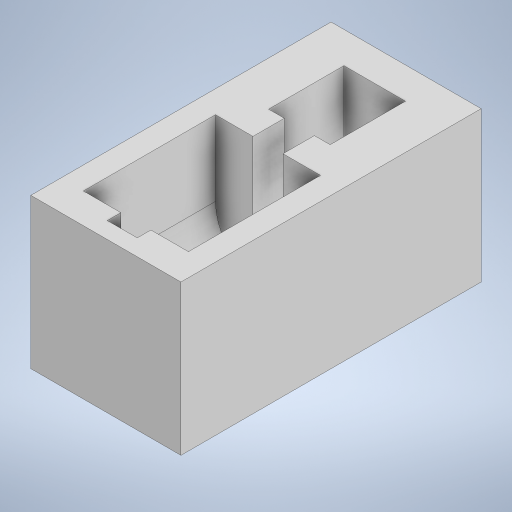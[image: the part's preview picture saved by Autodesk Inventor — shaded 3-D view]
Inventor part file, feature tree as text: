
AUTODESK INVENTOR PART (.ipt)
format: ipt  version: 2023 (Build 270158000, 158)  size: 318,464 bytes
history: native  units: in
note: dims shown in document units (in); Inventor stores cm internally (conversion verified against a paired STEP export)
features: extrude x9, plane x7, sketch x6, projected_geometry x4
ambient origin geometry x8: Origin, YZ Plane, XZ Plane, XY Plane, X Axis, Y Axis, Z Axis, Center Point
bodies: Solid1 (feature_tree)
feature tree (26):
  sketch  "Sketch1"  dims[d0=1.9685in d1=3.937in]
  extrude  "Extrusion1"  Depth=3.937in
  plane  "Work Plane3"
  plane  "Work Plane4"
  sketch  "Sketch3"  dims[d4=1.7323in d5=90.0deg]
  plane  "Work Plane5"
  plane  "Work Plane6"
  plane  "Work Plane7"
  extrude  "Extrusion5"  TaperAngle=90.0deg  [1 undecoded]
  extrude  "Extrusion6"  Depth=0.3937in
  sketch  "Sketch4"  dims[d6=1.378in d7=0.3937in]
  plane  "Work Plane8"
  extrude  "Extrusion7"  TaperAngle=90.0deg  [1 undecoded]
  extrude  "Extrusion8"  Depth=1.9685in TaperAngle=0.0deg
  extrude  "Extrusion9"  TaperAngle=90.0deg  [1 undecoded]
  extrude  "Extrusion10"  Depth=0.3937in TaperAngle=0.0deg
  plane  "Work Plane9"
  extrude  "Extrusion11"  Depth=0.3937in TaperAngle=0.0deg
  extrude  "Extrusion12"  Depth=1.378in
  projected_geometry  "Projected Loop2"
  projected_geometry  "Projected Loop3"
  sketch  "Sketch5"  dims[d8=0.9882in d9=90.0deg]
  projected_geometry  "Projected Loop4"
  sketch  "Sketch6"  dims[d10=0.8071in d11=1.9685in d12=0.0in]
  projected_geometry  "Projected Loop5"
  sketch  "Sketch7"  dims[d18=0.7953in d21=90.0deg d22=0.3937in d23=0.0in d24=0.3937in d25=0.0in d26=1.378in d27=90.0deg d28=0.3937in d29=0.0in d30=0.3937in d31=0.0in d32=0.3937in d33=2.3228in d34=0.0in d35=0.1969in d36=90.0deg d37=0.0in d38=0.0in d39=0.0in d40=0.0in d41=0.0in d42=0.7874in d43=0.3937in d44=0.1969in d45=0.7874in d46=0.3937in d47=0.0in]
note: 3 required parameter values undecoded (feature->parameter linkage not recoverable at this tier; creation-order binding heuristic only, values carry confidence <= 0.55)
